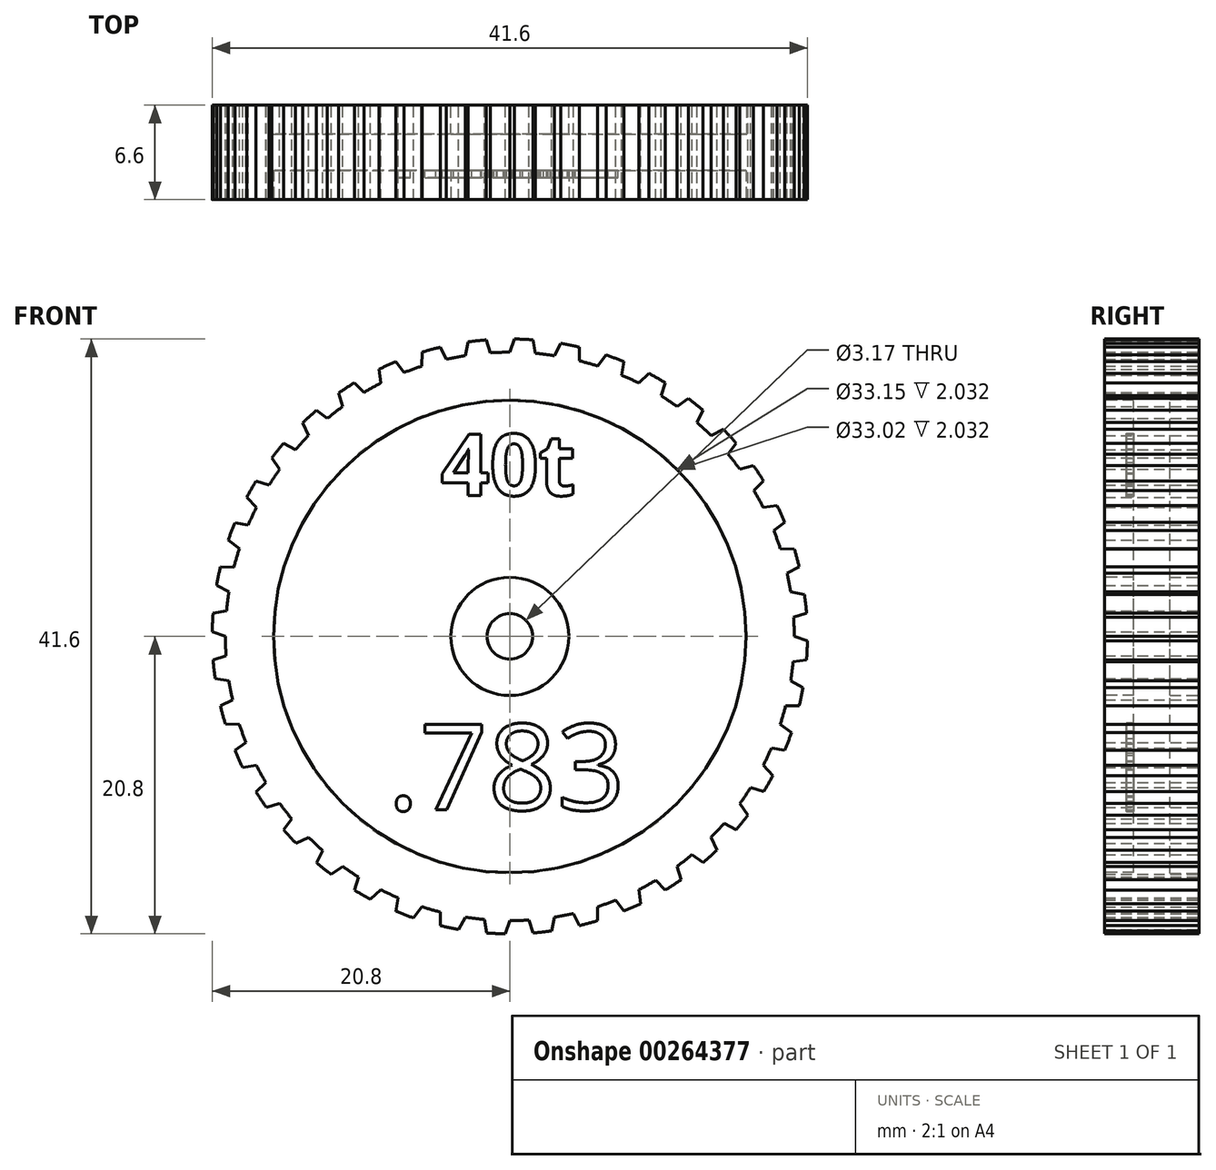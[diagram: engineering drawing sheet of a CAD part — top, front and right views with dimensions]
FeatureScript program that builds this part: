
annotation { "Feature Type Name" : "Feature", "Feature Type Description" : "" }
export const myFeature = defineFeature(function(context is Context, id is Id, definition is map)
    precondition{}
    {
        {
            var Q0;
            Q0=qCreatedBy(makeId("Front.planeOp"),FACE);
            var sketch = newSketch(context, id + "F0", { "sketchPlane" : qUnion([Q0])});
            skCircle(sketch, "E0", {"center": v(0, 0) * mm, "radius": 19.88 * mm});
            skCircle(sketch, "E1", {"center": v(0, 0) * mm, "radius": 1.59 * mm});
            skSolve(sketch);
        }
        {
            var Q0;
            Q0=qSketchRegion(id+"F0",true);
            extrude(context, id + "F1", {"entities" : qUnion([Q0]), "depth" : 6.6 * mm});
        }
        {
            var Q0;
            Q0=qCreatedBy(makeId("Front.planeOp"),FACE);
            var sketch = newSketch(context, id + "F2", { "sketchPlane" : qUnion([Q0])});
            skCircle(sketch, "E2", {"center": v(0, 0) * mm, "radius": 4.13 * mm});
            skCircle(sketch, "E3", {"center": v(0, 0) * mm, "radius": 16.57 * mm});
            skSolve(sketch);
        }
        {
            var Q0;
            Q0=qSketchRegion(id+"F2",true);
            extrude(context, id + "F3", {"entities" : qUnion([Q0]), "operationType" : NewBodyOperationType.REMOVE, "depth" : 2.03 * mm});
        }
        {
            var Q0;
            Q0=makeQuery(id+"F1.opExtrude","CAP_FACE",FACE,{"disambiguationData":[OSD([sQuery(id+"F0.wireOp",EDGE,"E0"),sQuery(id+"F0.wireOp",EDGE,"E1")])],"isStart":false});
            var sketch = newSketch(context, id + "F4", { "sketchPlane" : qUnion([Q0])});
            skCircle(sketch, "E4", {"center": v(0, 0) * mm, "radius": 4.13 * mm});
            skCircle(sketch, "E5", {"center": v(0, 0) * mm, "radius": 16.51 * mm});
            skSolve(sketch);
        }
        {
            var Q0;
            Q0=qSketchRegion(id+"F4",true);
            extrude(context, id + "F5", {"entities" : qUnion([Q0]), "operationType" : NewBodyOperationType.REMOVE, "oppositeDirection" : true, "depth" : 2.03 * mm});
        }
        {
            var Q0;
            Q0=qCreatedBy(makeId("Top.planeOp"),FACE);
            var sketch = newSketch(context, id + "F6", { "sketchPlane" : qUnion([Q0])});
            skLineSegment(sketch, "E6", {"start": v(0, 0) * mm, "end": v(0, -9.07) * mm, "construction": true});
            skSolve(sketch);
        }
        {
            var Q0;
            Q0=qCreatedBy(makeId("Front.planeOp"),FACE);
            var sketch = newSketch(context, id + "F7", { "sketchPlane" : qUnion([Q0])});
            skLineSegment(sketch, "E7", {"start": v(0, 0.03) * mm, "end": v(0, 22.57) * mm, "construction": true});
            skLineSegment(sketch, "E8", {"start": v(0, 0.03) * mm, "end": v(3.53, 22.32) * mm, "construction": true});
            skLineSegment(sketch, "E9", {"start": v(0, 0.03) * mm, "end": v(1.78, 22.7) * mm, "construction": true});
            skPoint(sketch, "E10.center", {"position": v(0, 0.03) * mm});
            skLineSegment(sketch, "E10.anchor1", {"start": v(0, 0.03) * mm, "end": v(0, 20.4) * mm, "construction": true});
            skLineSegment(sketch, "E10.anchor2", {"start": v(0, 0.03) * mm, "end": v(0, 20.4) * mm, "construction": true});
            skArc(sketch, "E11", {"start": v(1.63, 20.73) * mm, "mid": v(0.98, 20.78) * mm, "end": v(0.32, 20.8) * mm});
            skArc(sketch, "E12.0", {"start": v(1.77, 19.8) * mm, "mid": v(0.89, 19.86) * mm, "end": v(0, 19.88) * mm});
            skLineSegment(sketch, "E13", {"start": v(0, 19.88) * mm, "end": v(0.32, 20.8) * mm});
            skLineSegment(sketch, "E14", {"start": v(1.63, 20.73) * mm, "end": v(1.77, 19.8) * mm});
            skSolve(sketch);
        }
        {
            var Q0;
            Q0=qSketchRegion(id+"F7",true);
            var Q1;
            {var subQ0=sQuery(id+"F0.wireOp",EDGE,"E0");Q1=makeQuery(id+"F5.boolean.opBoolean","SPLIT",FACE,{"disambiguationData":[TD([makeQuery(id+"F1.opExtrude","SWEPT_FACE",FACE,{"disambiguationData":[OSD([subQ0])]})])],"derivedFrom":makeQuery(id+"F1.opExtrude","CAP_FACE",FACE,{"disambiguationData":[OSD([subQ0,sQuery(id+"F0.wireOp",EDGE,"E1")])],"isStart":false})});}
            extrude(context, id + "F8", {"entities" : qUnion([Q0]), "endBound" : BoundingType.UP_TO_SURFACE, "endBoundEntityFace" : qUnion([Q1]), "depth" : 25.4 * mm});
        }
        {
            var Q0;
            Q0=makeQuery(id+"F8.opExtrude","SWEPT_BODY",BODY,{"disambiguationData":[OSD([sQuery(id+"F7.wireOp",EDGE,"E11"),sQuery(id+"F7.wireOp",EDGE,"E12.0"),sQuery(id+"F7.wireOp",EDGE,"E13"),sQuery(id+"F7.wireOp",EDGE,"E14")])]});
            var Q1;
            Q1=sQuery(id+"F6.wireOp",EDGE,"E6");
            circularPattern(context, id + "F9", {"operationType" : NewBodyOperationType.ADD, "entities" : qUnion([Q0]), "axis" : qUnion([Q1]), "angle" : 9 * degree, "instanceCount" : round(40)});
        }
        {
            var Q0;
            Q0=makeQuery(id+"F5.boolean.opBoolean","COPY",FACE,{"derivedFrom":makeQuery(id+"F5.opExtrude","CAP_FACE",FACE,{"disambiguationData":[OSD([sQuery(id+"F4.wireOp",EDGE,"E4"),sQuery(id+"F4.wireOp",EDGE,"E5")])],"isStart":false})});
            var sketch = newSketch(context, id + "F10", { "sketchPlane" : qUnion([Q0])});
            skText(sketch, "E15", { "text": "40t", "fontName": "OpenSans-Bold.ttf"});
            skText(sketch, "E16", { "text": ".783", "fontName": "OpenSans-Regular.ttf"});
            const initialGuessF10  = {"E15": [-0.00483, 0.00986, 1, 0, 0.00431], "E16": [-0.00856, -0.01213, 1, 0, 0.00604]};
            skSetInitialGuess(sketch, initialGuessF10);
            skSolve(sketch);
        }
        {
            var Q0;
            Q0=qSketchRegion(id+"F10",true);
            extrude(context, id + "F11", {"entities" : qUnion([Q0]), "operationType" : NewBodyOperationType.ADD, "depth" : 0.5 * mm});
        }
    });
